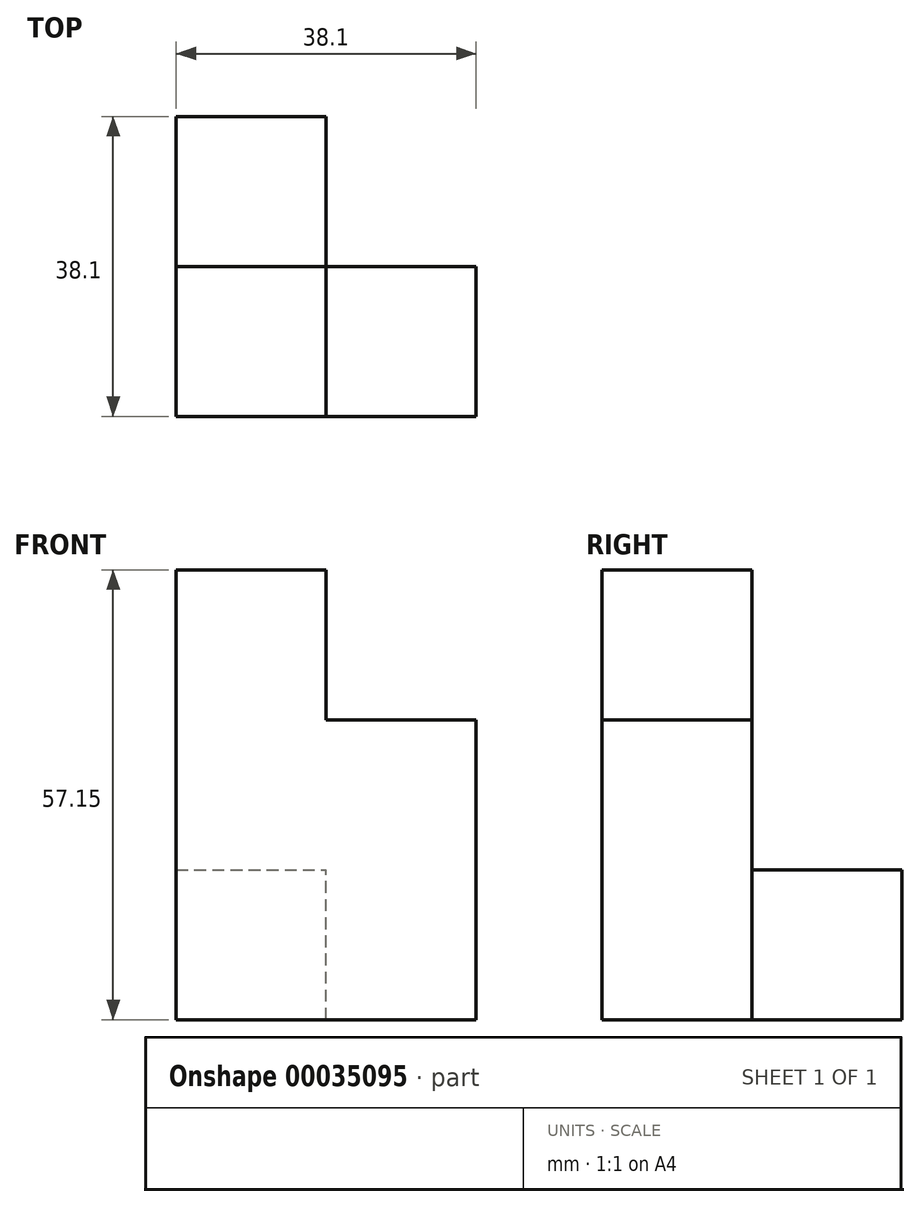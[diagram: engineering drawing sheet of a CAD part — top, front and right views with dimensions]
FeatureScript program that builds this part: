
annotation { "Feature Type Name" : "Feature", "Feature Type Description" : "" }
export const myFeature = defineFeature(function(context is Context, id is Id, definition is map)
    precondition{}
    {
        {
            var Q0;
            Q0=qCreatedBy(makeId("Top.planeOp"),FACE);
            var sketch = newSketch(context, id + "F0", { "sketchPlane" : qUnion([Q0])});
            skLineSegment(sketch, "E0.bottom", {"start": v(0, 0) * mm, "end": v(19.05, 0) * mm});
            skLineSegment(sketch, "E0.top", {"start": v(0, 19.05) * mm, "end": v(19.05, 19.05) * mm});
            skLineSegment(sketch, "E0.left", {"start": v(0, 0) * mm, "end": v(0, 19.05) * mm});
            skLineSegment(sketch, "E0.right", {"start": v(19.05, 0) * mm, "end": v(19.05, 19.05) * mm});
            skSolve(sketch);
        }
        {
            var Q0;
            Q0 = qSketchRegion(id + "F0", true);
            extrude(context, id + "F1", {"entities" : qUnion([Q0]), "depth" : 19.05 * mm});
        }
        {
            var Q0;
            Q0=makeQuery(id+"F1.opExtrude","CAP_FACE",FACE,{"disambiguationData":[OSD([sQuery(id+"F0.wireOp",EDGE,"E0.bottom"),sQuery(id+"F0.wireOp",EDGE,"E0.top"),sQuery(id+"F0.wireOp",EDGE,"E0.left"),sQuery(id+"F0.wireOp",EDGE,"E0.right")])],"isStart":false});
            var sketch = newSketch(context, id + "F2", { "sketchPlane" : qUnion([Q0])});
            skLineSegment(sketch, "E1.bottom", {"start": v(0, 0) * mm, "end": v(19.05, 0) * mm});
            skLineSegment(sketch, "E1.top", {"start": v(0, 19.05) * mm, "end": v(19.05, 19.05) * mm});
            skLineSegment(sketch, "E1.left", {"start": v(0, 0) * mm, "end": v(0, 19.05) * mm});
            skLineSegment(sketch, "E1.right", {"start": v(19.05, 0) * mm, "end": v(19.05, 19.05) * mm});
            skSolve(sketch);
        }
        {
            var Q0;
            Q0=makeQuery(id+"F2.imprint","IMPRINT",FACE,{"disambiguationData":[TD([[makeQuery(id+"F2.imprint","IMPRINT",EDGE,{"derivedFrom":sQuery(id+"F2.wireOp",EDGE,"E1.bottom")}),1.0]])]});
            extrude(context, id + "F3", {"entities" : qUnion([Q0]), "operationType" : NewBodyOperationType.ADD, "depth" : 19.05 * mm});
        }
        {
            var Q0;
            Q0=makeQuery(id+"F3.boolean.opBoolean","MERGE",FACE,{"derivedFrom":[makeQuery(id+"F1.opExtrude","SWEPT_FACE",FACE,{"disambiguationData":[OSD([sQuery(id+"F0.wireOp",EDGE,"E0.right")])]}),makeQuery(id+"F3.opExtrude","SWEPT_FACE",FACE,{"disambiguationData":[OSD([sQuery(id+"F2.wireOp",EDGE,"E1.right")])]})]});
            var sketch = newSketch(context, id + "F4", { "sketchPlane" : qUnion([Q0])});
            skLineSegment(sketch, "E2.bottom", {"start": v(0, 0) * mm, "end": v(19.05, 0) * mm});
            skLineSegment(sketch, "E2.top", {"start": v(0, 38.1) * mm, "end": v(19.05, 38.1) * mm});
            skLineSegment(sketch, "E2.left", {"start": v(0, 0) * mm, "end": v(0, 38.1) * mm});
            skLineSegment(sketch, "E2.right", {"start": v(19.05, 0) * mm, "end": v(19.05, 38.1) * mm});
            skSolve(sketch);
        }
        {
            var Q0;
            Q0=makeQuery(id+"F4.imprint","IMPRINT",FACE,{"disambiguationData":[TD([[makeQuery(id+"F4.imprint","IMPRINT",EDGE,{"derivedFrom":sQuery(id+"F4.wireOp",EDGE,"E2.bottom")}),1.0]])]});
            extrude(context, id + "F5", {"entities" : qUnion([Q0]), "operationType" : NewBodyOperationType.ADD, "depth" : 19.05 * mm});
        }
        {
            var Q0;
            Q0=makeQuery(id+"F5.boolean.opBoolean","MERGE",FACE,{"derivedFrom":[makeQuery(id+"F3.opExtrude","CAP_FACE",FACE,{"disambiguationData":[OSD([sQuery(id+"F2.wireOp",EDGE,"E1.bottom"),sQuery(id+"F2.wireOp",EDGE,"E1.top"),sQuery(id+"F2.wireOp",EDGE,"E1.left"),sQuery(id+"F2.wireOp",EDGE,"E1.right")])],"isStart":false}),makeQuery(id+"F5.opExtrude","SWEPT_FACE",FACE,{"disambiguationData":[OSD([sQuery(id+"F4.wireOp",EDGE,"E2.top")])]})]});
            var sketch = newSketch(context, id + "F6", { "sketchPlane" : qUnion([Q0])});
            skLineSegment(sketch, "E3.bottom", {"start": v(0, 0) * mm, "end": v(19.05, 0) * mm});
            skLineSegment(sketch, "E3.top", {"start": v(0, 19.05) * mm, "end": v(19.05, 19.05) * mm});
            skLineSegment(sketch, "E3.left", {"start": v(0, 0) * mm, "end": v(0, 19.05) * mm});
            skLineSegment(sketch, "E3.right", {"start": v(19.05, 0) * mm, "end": v(19.05, 19.05) * mm});
            skSolve(sketch);
        }
        {
            var Q0;
            Q0=makeQuery(id+"F6.imprint","IMPRINT",FACE,{"disambiguationData":[TD([[makeQuery(id+"F6.imprint","IMPRINT",EDGE,{"derivedFrom":sQuery(id+"F6.wireOp",EDGE,"E3.bottom")}),1.0]])]});
            extrude(context, id + "F7", {"entities" : qUnion([Q0]), "operationType" : NewBodyOperationType.ADD, "depth" : 19.05 * mm});
        }
        {
            var Q0;
            Q0=makeQuery(id+"F7.boolean.opBoolean","MERGE",FACE,{"derivedFrom":[makeQuery(id+"F5.boolean.opBoolean","MERGE",FACE,{"derivedFrom":[makeQuery(id+"F3.boolean.opBoolean","MERGE",FACE,{"derivedFrom":[makeQuery(id+"F1.opExtrude","SWEPT_FACE",FACE,{"disambiguationData":[OSD([sQuery(id+"F0.wireOp",EDGE,"E0.top")])]}),makeQuery(id+"F3.opExtrude","SWEPT_FACE",FACE,{"disambiguationData":[OSD([sQuery(id+"F2.wireOp",EDGE,"E1.top")])]})]}),makeQuery(id+"F5.opExtrude","SWEPT_FACE",FACE,{"disambiguationData":[OSD([sQuery(id+"F4.wireOp",EDGE,"E2.right")])]})]}),makeQuery(id+"F7.opExtrude","SWEPT_FACE",FACE,{"disambiguationData":[OSD([sQuery(id+"F6.wireOp",EDGE,"E3.top")])]})]});
            var sketch = newSketch(context, id + "F8", { "sketchPlane" : qUnion([Q0])});
            skLineSegment(sketch, "E4.bottom", {"start": v(0, 0) * mm, "end": v(-19.05, 0) * mm});
            skLineSegment(sketch, "E4.top", {"start": v(0, 19.05) * mm, "end": v(-19.05, 19.05) * mm});
            skLineSegment(sketch, "E4.left", {"start": v(0, 0) * mm, "end": v(0, 19.05) * mm});
            skLineSegment(sketch, "E4.right", {"start": v(-19.05, 0) * mm, "end": v(-19.05, 19.05) * mm});
            skSolve(sketch);
        }
        {
            var Q0;
            Q0=makeQuery(id+"F8.imprint","IMPRINT",FACE,{"disambiguationData":[TD([[makeQuery(id+"F8.imprint","IMPRINT",EDGE,{"derivedFrom":sQuery(id+"F8.wireOp",EDGE,"E4.bottom")}),-1.0]])]});
            extrude(context, id + "F9", {"entities" : qUnion([Q0]), "operationType" : NewBodyOperationType.ADD, "depth" : 19.05 * mm});
        }
    });
